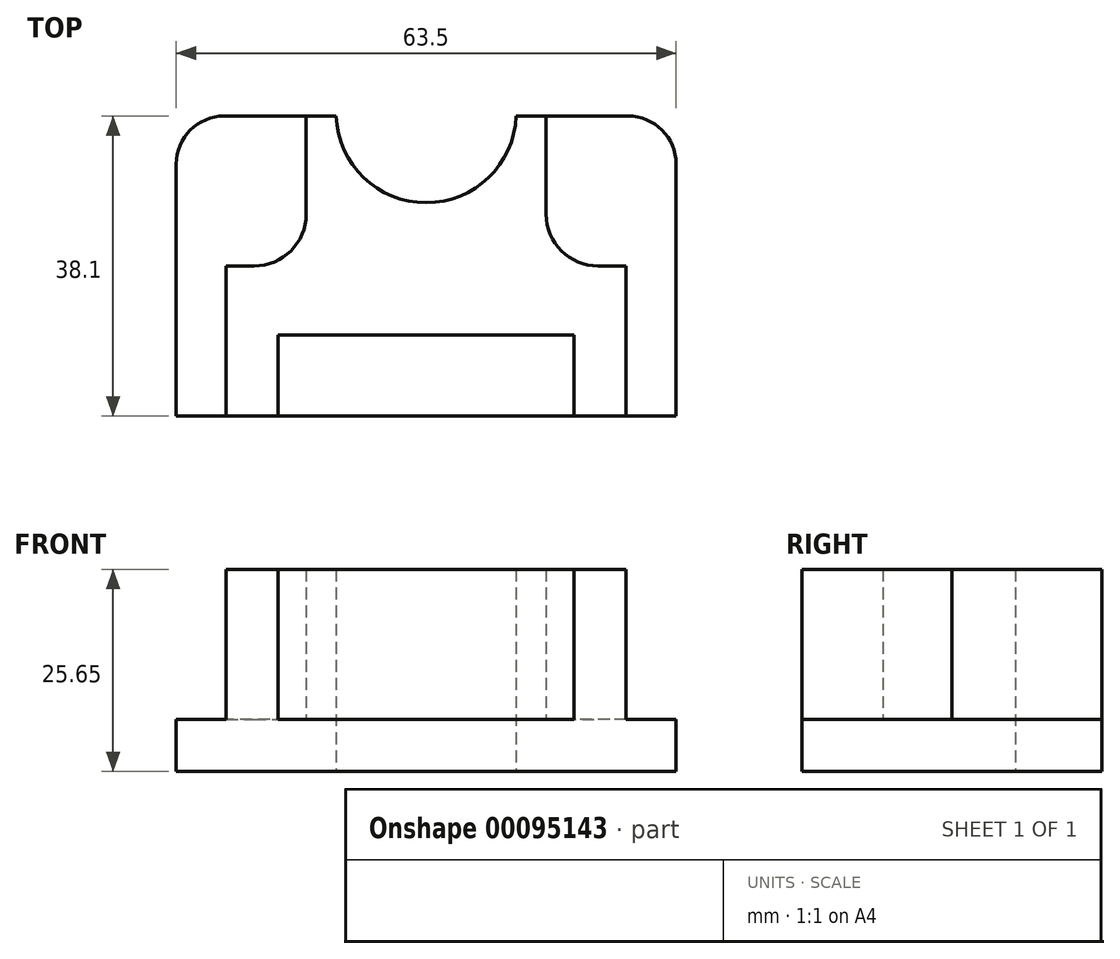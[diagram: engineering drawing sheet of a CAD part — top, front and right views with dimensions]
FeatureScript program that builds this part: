
annotation { "Feature Type Name" : "Feature", "Feature Type Description" : "" }
export const myFeature = defineFeature(function(context is Context, id is Id, definition is map)
    precondition{}
    {
        {
            var Q0;
            Q0=qCreatedBy(makeId("Top.planeOp"),FACE);
            var sketch = newSketch(context, id + "F0", { "sketchPlane" : qUnion([Q0])});
            skLineSegment(sketch, "E0.bottom", {"start": v(25.65, 19.05) * mm, "end": v(-25.65, 19.05) * mm});
            skLineSegment(sketch, "E0.top", {"start": v(31.75, -19.05) * mm, "end": v(-31.75, -19.05) * mm});
            skLineSegment(sketch, "E0.left", {"start": v(31.75, 12.95) * mm, "end": v(31.75, -19.05) * mm});
            skLineSegment(sketch, "E0.right", {"start": v(-31.75, 12.95) * mm, "end": v(-31.75, -19.05) * mm});
            skPoint(sketch, "E0.middle", {"position": v(0, 0) * mm});
            skPoint(sketch, "E1.visualSharp", {"position": v(-31.75, 19.05) * mm});
            skArc(sketch, "E1.filletArc", {"start": v(-25.65, 19.05) * mm, "mid": v(-29.96, 17.26) * mm, "end": v(-31.75, 12.95) * mm});
            skPoint(sketch, "E2.visualSharp", {"position": v(31.75, 19.05) * mm});
            skArc(sketch, "E2.filletArc", {"start": v(31.75, 12.95) * mm, "mid": v(29.96, 17.26) * mm, "end": v(25.65, 19.05) * mm});
            skSolve(sketch);
        }
        {
            var Q0;
            Q0=makeQuery(id+"F0.imprint","IMPRINT",FACE,{"disambiguationData":[TD([[makeQuery(id+"F0.imprint","IMPRINT",EDGE,{"derivedFrom":sQuery(id+"F0.wireOp",EDGE,"E0.bottom")}),1.0]])]});
            extrude(context, id + "F1", {"entities" : qUnion([Q0]), "depth" : 6.6 * mm});
        }
        {
            var Q0;
            Q0=makeQuery(id+"F1.opExtrude","CAP_FACE",FACE,{"disambiguationData":[OSD([sQuery(id+"F0.wireOp",EDGE,"E0.bottom"),sQuery(id+"F0.wireOp",EDGE,"E0.top"),sQuery(id+"F0.wireOp",EDGE,"E0.left"),sQuery(id+"F0.wireOp",EDGE,"E0.right"),sQuery(id+"F0.wireOp",EDGE,"E1.filletArc"),sQuery(id+"F0.wireOp",EDGE,"E2.filletArc")])],"isStart":false});
            var sketch = newSketch(context, id + "F2", { "sketchPlane" : qUnion([Q0])});
            skLineSegment(sketch, "E3", {"start": v(-18.8, -19.05) * mm, "end": v(-25.4, -19.05) * mm});
            skLineSegment(sketch, "E4", {"start": v(-25.4, -19.05) * mm, "end": v(-25.4, 0) * mm});
            skLineSegment(sketch, "E5", {"start": v(-25.4, 0) * mm, "end": v(-21.84, 0) * mm});
            skLineSegment(sketch, "E6", {"start": v(-15.24, 6.6) * mm, "end": v(-15.24, 19.05) * mm});
            skLineSegment(sketch, "E7", {"start": v(-15.24, 19.05) * mm, "end": v(-11.43, 19.05) * mm});
            skLineSegment(sketch, "E8", {"start": v(-18.8, -19.05) * mm, "end": v(-18.8, -8.75) * mm});
            skLineSegment(sketch, "E9", {"start": v(-18.8, -8.75) * mm, "end": v(0, -8.75) * mm});
            skLineSegment(sketch, "E10", {"start": v(0, 30.42) * mm, "end": v(0, -28.4) * mm, "construction": true});
            skPoint(sketch, "E10.endSnap0", {"position": v(0, 19.05) * mm});
            skLineSegment(sketch, "E11.MirrorCS", {"start": v(15.24, 19.05) * mm, "end": v(11.43, 19.05) * mm});
            skLineSegment(sketch, "E12.MirrorCS", {"start": v(15.24, 6.6) * mm, "end": v(15.24, 19.05) * mm});
            skLineSegment(sketch, "E13.MirrorCS", {"start": v(25.4, 0) * mm, "end": v(21.84, 0) * mm});
            skLineSegment(sketch, "E14.MirrorCS", {"start": v(25.4, -19.05) * mm, "end": v(25.4, 0) * mm});
            skLineSegment(sketch, "E15.MirrorCS", {"start": v(18.8, -19.05) * mm, "end": v(25.4, -19.05) * mm});
            skLineSegment(sketch, "E16.MirrorCS", {"start": v(18.8, -19.05) * mm, "end": v(18.8, -8.75) * mm});
            skLineSegment(sketch, "E17.MirrorCS", {"start": v(18.8, -8.75) * mm, "end": v(0, -8.75) * mm});
            skArc(sketch, "E18", {"start": v(-11.43, 19.05) * mm, "mid": v(0, 8.04) * mm, "end": v(11.43, 19.05) * mm});
            skPoint(sketch, "E19.visualSharp", {"position": v(-15.24, 0) * mm});
            skArc(sketch, "E19.filletArc", {"start": v(-21.84, 0) * mm, "mid": v(-17.17, 1.93) * mm, "end": v(-15.24, 6.6) * mm});
            skPoint(sketch, "E20.visualSharp", {"position": v(15.24, 0) * mm});
            skArc(sketch, "E20.filletArc", {"start": v(15.24, 6.6) * mm, "mid": v(17.17, 1.93) * mm, "end": v(21.84, 0) * mm});
            skSolve(sketch);
        }
        {
            var Q0;
            Q0 = qSketchRegion(id + "F2", true);
            extrude(context, id + "F3", {"entities" : qUnion([Q0]), "operationType" : NewBodyOperationType.ADD, "depth" : 19.05 * mm});
        }
        {
            var Q0;
            {var subQ0=sQuery(id+"F0.wireOp",EDGE,"E0.bottom");Q0=makeQuery(id+"F3.boolean.opBoolean","SPLIT",FACE,{"disambiguationData":[TD([makeQuery(id+"F3.opExtrude","SWEPT_FACE",FACE,{"disambiguationData":[OSD([sQuery(id+"F2.wireOp",EDGE,"E18")])]})])],"derivedFrom":makeQuery(id+"F1.opExtrude","CAP_FACE",FACE,{"disambiguationData":[OSD([subQ0,sQuery(id+"F0.wireOp",EDGE,"E0.top"),sQuery(id+"F0.wireOp",EDGE,"E0.left"),sQuery(id+"F0.wireOp",EDGE,"E0.right"),sQuery(id+"F0.wireOp",EDGE,"E1.filletArc"),sQuery(id+"F0.wireOp",EDGE,"E2.filletArc")])],"isStart":false})});}
            extrude(context, id + "F4", {"entities" : qUnion([Q0]), "operationType" : NewBodyOperationType.REMOVE, "oppositeDirection" : true, "depth" : 25.4 * mm});
        }
    });
